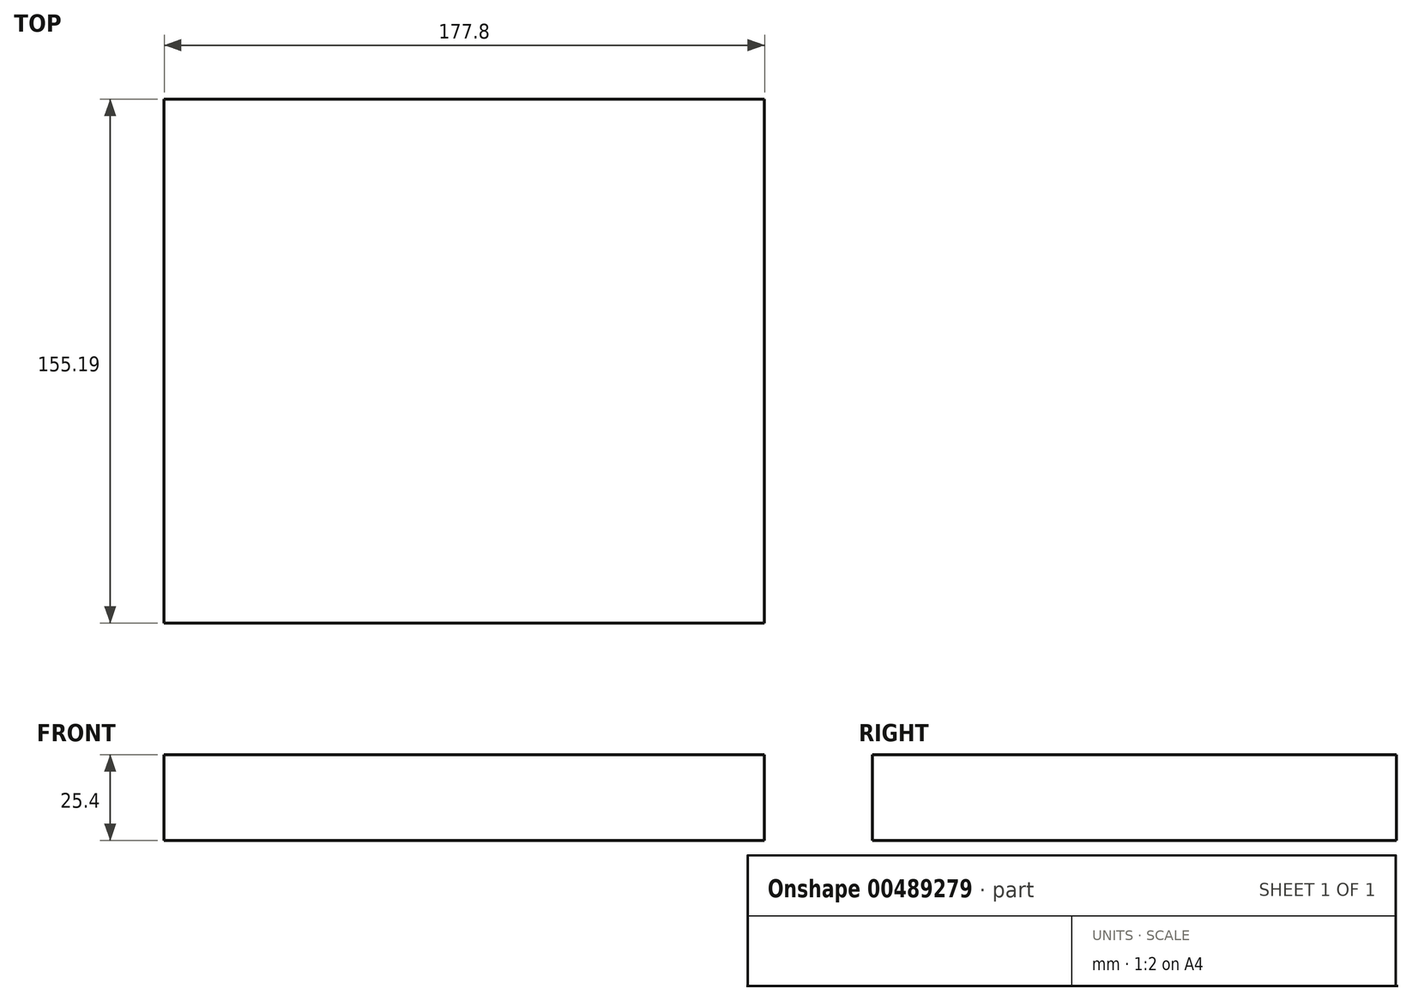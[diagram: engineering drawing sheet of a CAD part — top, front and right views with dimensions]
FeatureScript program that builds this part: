
annotation { "Feature Type Name" : "Feature", "Feature Type Description" : "" }
export const myFeature = defineFeature(function(context is Context, id is Id, definition is map)
    precondition{}
    {
        {
            var Q0;
            Q0=qCreatedBy(makeId("Front.planeOp"),FACE);
            var sketch = newSketch(context, id + "F0", { "sketchPlane" : qUnion([Q0])});
            skLineSegment(sketch, "E0.bottom", {"start": v(-14, 0) * mm, "end": v(163.8, 0) * mm});
            skLineSegment(sketch, "E0.top", {"start": v(-14, 25.4) * mm, "end": v(163.8, 25.4) * mm});
            skLineSegment(sketch, "E0.left", {"start": v(-14, 0) * mm, "end": v(-14, 25.4) * mm});
            skLineSegment(sketch, "E0.right", {"start": v(163.8, 0) * mm, "end": v(163.8, 25.4) * mm});
            skSolve(sketch);
        }
        {
            var Q0;
            Q0=makeQuery(id+"F0.imprint","IMPRINT",FACE,{"disambiguationData":[TD([[makeQuery(id+"F0.imprint","IMPRINT",EDGE,{"derivedFrom":sQuery(id+"F0.wireOp",EDGE,"E0.bottom")}),1.0]])]});
            extrude(context, id + "F1", {"entities" : qUnion([Q0]), "depth" : 155.2 * mm});
        }
    });
